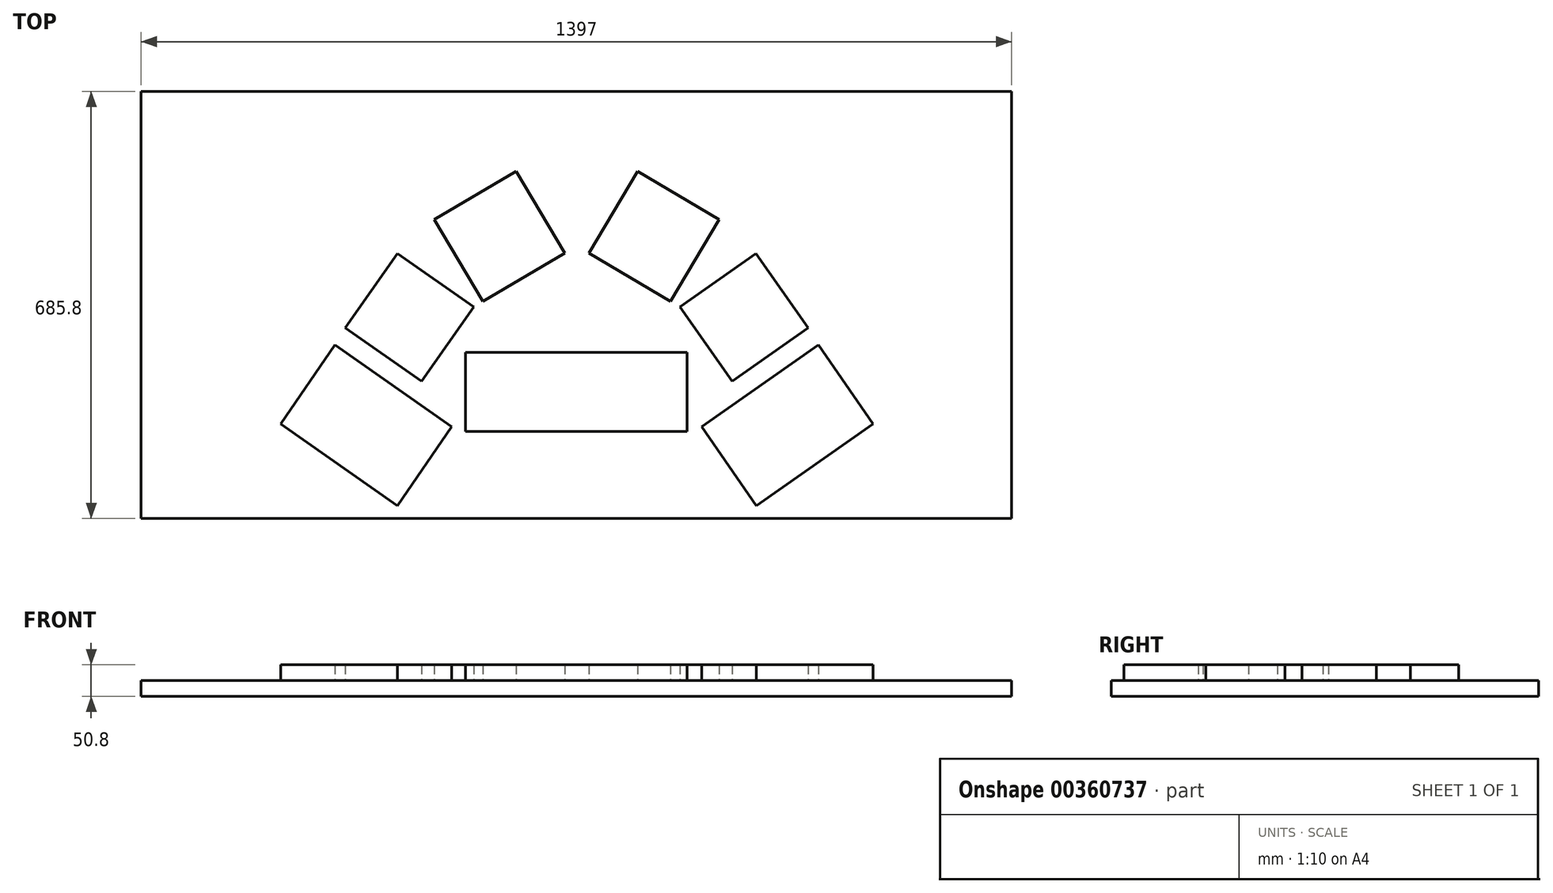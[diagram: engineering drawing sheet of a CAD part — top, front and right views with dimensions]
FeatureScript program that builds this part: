
annotation { "Feature Type Name" : "Feature", "Feature Type Description" : "" }
export const myFeature = defineFeature(function(context is Context, id is Id, definition is map)
    precondition{}
    {
        {
            var Q0;
            Q0=qCreatedBy(makeId("Top.planeOp"),FACE);
            var sketch = newSketch(context, id + "F0", { "sketchPlane" : qUnion([Q0])});
            skLineSegment(sketch, "E0.bottom", {"start": v(698.5, 342.9) * mm, "end": v(-698.5, 342.9) * mm});
            skLineSegment(sketch, "E0.top", {"start": v(698.5, -342.9) * mm, "end": v(-698.5, -342.9) * mm});
            skLineSegment(sketch, "E0.left", {"start": v(698.5, 342.9) * mm, "end": v(698.5, -342.9) * mm});
            skLineSegment(sketch, "E0.right", {"start": v(-698.5, 342.9) * mm, "end": v(-698.5, -342.9) * mm});
            skPoint(sketch, "E0.middle", {"position": v(0, 0) * mm});
            skSolve(sketch);
        }
        {
            var Q0;
            Q0 = qSketchRegion(id + "F0", true);
            extrude(context, id + "F1", {"entities" : qUnion([Q0]), "depth" : 25.4 * mm});
        }
        {
            var Q0;
            Q0=makeQuery(id+"F1.opExtrude","CAP_FACE",FACE,{"disambiguationData":[OSD([sQuery(id+"F0.wireOp",EDGE,"E0.bottom"),sQuery(id+"F0.wireOp",EDGE,"E0.top"),sQuery(id+"F0.wireOp",EDGE,"E0.left"),sQuery(id+"F0.wireOp",EDGE,"E0.right")])],"isStart":false});
            var sketch = newSketch(context, id + "F2", { "sketchPlane" : qUnion([Q0])});
            skLineSegment(sketch, "E1.bottom", {"start": v(177.8, -76.2) * mm, "end": v(-177.8, -76.2) * mm});
            skLineSegment(sketch, "E1.top", {"start": v(177.8, -203.2) * mm, "end": v(-177.8, -203.2) * mm});
            skLineSegment(sketch, "E1.left", {"start": v(177.8, -76.2) * mm, "end": v(177.8, -203.2) * mm});
            skLineSegment(sketch, "E1.right", {"start": v(-177.8, -76.2) * mm, "end": v(-177.8, -203.2) * mm});
            skPoint(sketch, "E1.middle", {"position": v(0, -139.7) * mm});
            skLineSegment(sketch, "E2.bottom", {"start": v(-387.33, -64.26) * mm, "end": v(-200.08, -195.38) * mm});
            skLineSegment(sketch, "E2.top", {"start": v(-474.75, -191.26) * mm, "end": v(-287.49, -322.38) * mm});
            skLineSegment(sketch, "E2.left", {"start": v(-387.33, -64.26) * mm, "end": v(-474.75, -191.26) * mm});
            skLineSegment(sketch, "E2.right", {"start": v(-200.08, -195.38) * mm, "end": v(-287.49, -322.38) * mm});
            skLineSegment(sketch, "E3.bottom", {"start": v(-287.13, 82.66) * mm, "end": v(-164.73, -3.05) * mm});
            skLineSegment(sketch, "E3.top", {"start": v(-370.9, -36.98) * mm, "end": v(-248.5, -122.69) * mm});
            skLineSegment(sketch, "E3.left", {"start": v(-287.13, 82.66) * mm, "end": v(-370.9, -36.98) * mm});
            skLineSegment(sketch, "E3.right", {"start": v(-164.73, -3.05) * mm, "end": v(-248.5, -122.69) * mm});
            skPoint(sketch, "E4", {"position": v(-243.78, -258.88) * mm});
            skPoint(sketch, "E5", {"position": v(-381.12, -258.88) * mm});
            skPoint(sketch, "E5.positionSnap0", {"position": v(-381.12, -256.82) * mm});
            skPoint(sketch, "E6", {"position": v(-293.7, -129.82) * mm});
            skPoint(sketch, "E7", {"position": v(-225.93, 39.8) * mm});
            skPoint(sketch, "E8", {"position": v(-309.7, -79.83) * mm});
            skPoint(sketch, "E9", {"position": v(-206.62, -62.87) * mm});
            skPoint(sketch, "E10", {"position": v(-263.28, -21.15) * mm});
            skPoint(sketch, "E11", {"position": v(-325.63, -200.62) * mm});
            skCircle(sketch, "E12.cCircle", {"center": v(0, 0) * mm, "radius": 50.85 * mm, "construction": true});
            skLineSegment(sketch, "E12.0", {"start": v(50.54, -29.89) * mm, "end": v(-0.61, -58.71) * mm, "construction": true});
            skLineSegment(sketch, "E12.1", {"start": v(-0.61, -58.71) * mm, "end": v(-51.15, -28.83) * mm, "construction": true});
            skLineSegment(sketch, "E12.2", {"start": v(-51.15, -28.83) * mm, "end": v(-50.54, 29.89) * mm, "construction": true});
            skLineSegment(sketch, "E12.3", {"start": v(-50.54, 29.89) * mm, "end": v(0.61, 58.71) * mm, "construction": true});
            skLineSegment(sketch, "E12.4", {"start": v(0.61, 58.71) * mm, "end": v(51.15, 28.83) * mm, "construction": true});
            skLineSegment(sketch, "E12.5", {"start": v(51.15, 28.83) * mm, "end": v(50.54, -29.89) * mm, "construction": true});
            skPoint(sketch, "E12.0.midPoint", {"position": v(24.96, -44.3) * mm});
            skPoint(sketch, "E13", {"position": v(0, -76.2) * mm});
            skPoint(sketch, "E14.endSnap0", {"position": v(0, -342.9) * mm});
            skLineSegment(sketch, "E15.bottom", {"start": v(-96.82, 214.72) * mm, "end": v(-18.8, 83.1) * mm});
            skLineSegment(sketch, "E15.top", {"start": v(-227.92, 137) * mm, "end": v(-149.9, 5.4) * mm});
            skLineSegment(sketch, "E15.left", {"start": v(-96.82, 214.72) * mm, "end": v(-227.92, 137) * mm});
            skLineSegment(sketch, "E15.right", {"start": v(-18.8, 83.1) * mm, "end": v(-149.9, 5.4) * mm});
            skLineSegment(sketch, "E16", {"start": v(0.61, 301.92) * mm, "end": v(0.61, -305.65) * mm});
            skPoint(sketch, "E17", {"position": v(-84.35, 44.25) * mm});
            skLineSegment(sketch, "E18.MirrorCS", {"start": v(98.05, 214.72) * mm, "end": v(20.02, 83.1) * mm});
            skLineSegment(sketch, "E19.MirrorCS", {"start": v(98.05, 214.72) * mm, "end": v(229.14, 137) * mm});
            skLineSegment(sketch, "E20.MirrorCS", {"start": v(20.02, 83.1) * mm, "end": v(151.12, 5.4) * mm});
            skLineSegment(sketch, "E21.MirrorCS", {"start": v(229.14, 137) * mm, "end": v(151.12, 5.4) * mm});
            skLineSegment(sketch, "E22.MirrorCS", {"start": v(288.36, 82.66) * mm, "end": v(165.95, -3.05) * mm});
            skLineSegment(sketch, "E23.MirrorCS", {"start": v(165.95, -3.05) * mm, "end": v(249.73, -122.69) * mm});
            skLineSegment(sketch, "E24.MirrorCS", {"start": v(372.13, -36.98) * mm, "end": v(249.73, -122.69) * mm});
            skLineSegment(sketch, "E25.MirrorCS", {"start": v(288.36, 82.66) * mm, "end": v(372.13, -36.98) * mm});
            skLineSegment(sketch, "E26.MirrorCS", {"start": v(388.56, -64.26) * mm, "end": v(475.97, -191.26) * mm});
            skLineSegment(sketch, "E27.MirrorCS", {"start": v(388.56, -64.26) * mm, "end": v(201.3, -195.38) * mm});
            skLineSegment(sketch, "E28.MirrorCS", {"start": v(475.97, -191.26) * mm, "end": v(288.71, -322.38) * mm});
            skLineSegment(sketch, "E29.MirrorCS", {"start": v(201.3, -195.38) * mm, "end": v(288.71, -322.38) * mm});
            skPoint(sketch, "E30", {"position": v(85.49, 44.3) * mm});
            skPoint(sketch, "E30.positionSnap0", {"position": v(-24.96, 44.3) * mm});
            skPoint(sketch, "E31", {"position": v(207.84, -62.87) * mm});
            skPoint(sketch, "E32", {"position": v(245, -258.88) * mm});
            skSolve(sketch);
        }
        {
            var Q0;
            Q0 = qSketchRegion(id + "F2", true);
            extrude(context, id + "F3", {"entities" : qUnion([Q0]), "depth" : 25.4 * mm});
        }
    });
